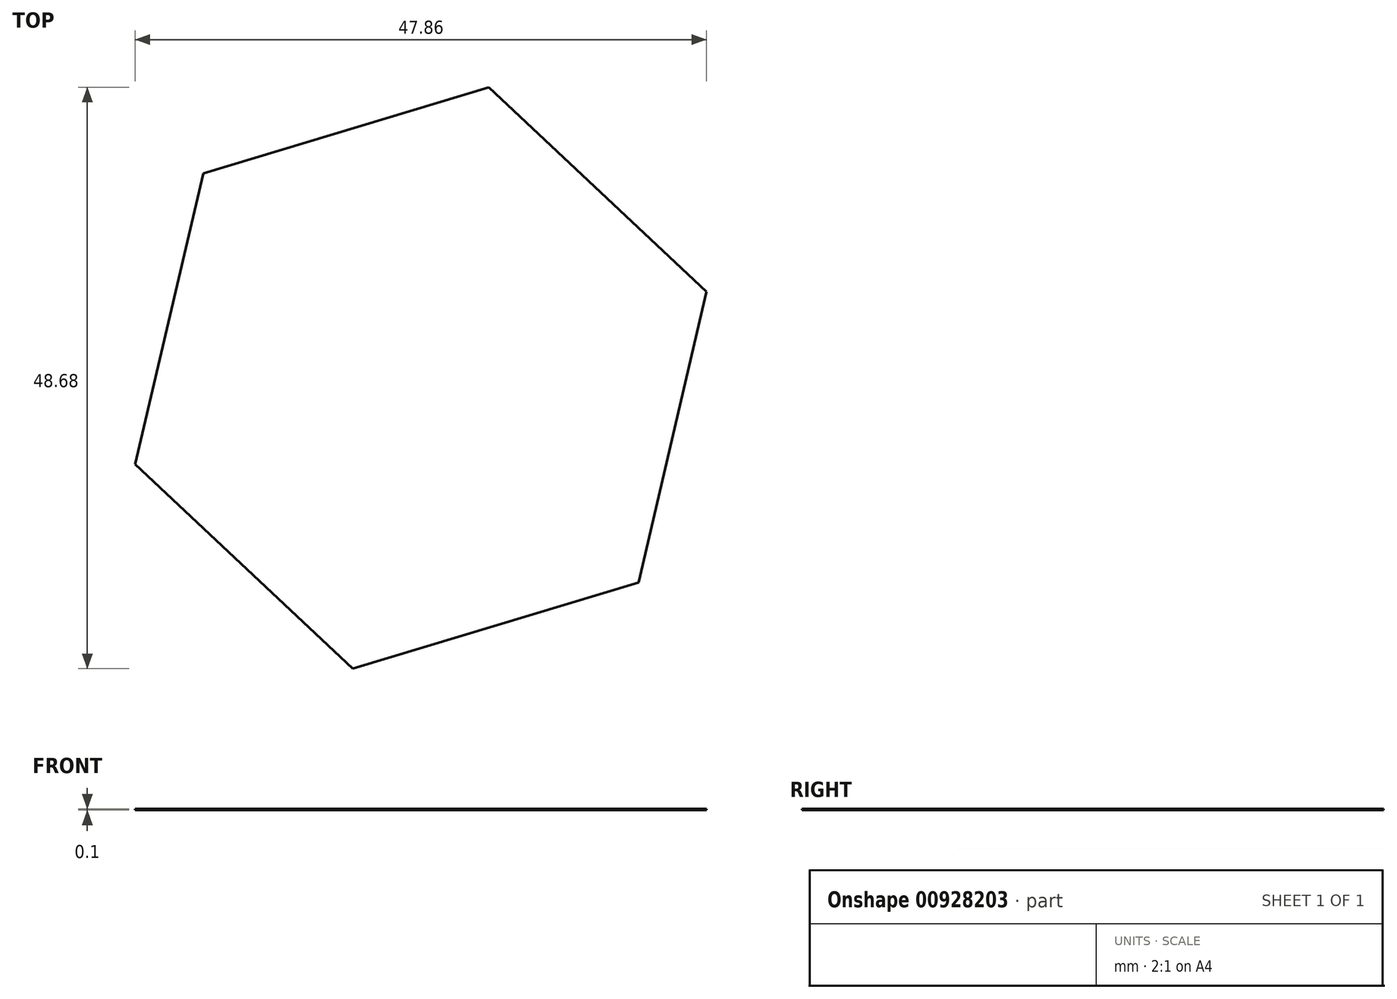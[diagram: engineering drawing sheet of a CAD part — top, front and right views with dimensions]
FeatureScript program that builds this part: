
annotation { "Feature Type Name" : "Feature", "Feature Type Description" : "" }
export const myFeature = defineFeature(function(context is Context, id is Id, definition is map)
    precondition{}
    {
        {
            var Q0;
            Q0=qCreatedBy(makeId("Top.planeOp"),FACE);
            var sketch = newSketch(context, id + "F0", { "sketchPlane" : qUnion([Q0])});
            skCircle(sketch, "E0.cCircle", {"center": v(0, 0) * mm, "radius": 21.65 * mm, "construction": true});
            skLineSegment(sketch, "E0.0", {"start": v(18.22, -17.11) * mm, "end": v(-5.71, -24.34) * mm});
            skLineSegment(sketch, "E0.1", {"start": v(-5.71, -24.34) * mm, "end": v(-23.93, -7.22) * mm});
            skLineSegment(sketch, "E0.2", {"start": v(-23.93, -7.22) * mm, "end": v(-18.22, 17.11) * mm});
            skLineSegment(sketch, "E0.3", {"start": v(-18.22, 17.11) * mm, "end": v(5.71, 24.34) * mm});
            skLineSegment(sketch, "E0.4", {"start": v(5.71, 24.34) * mm, "end": v(23.93, 7.22) * mm});
            skLineSegment(sketch, "E0.5", {"start": v(23.93, 7.22) * mm, "end": v(18.22, -17.11) * mm});
            skPoint(sketch, "E0.0.midPoint", {"position": v(6.26, -20.73) * mm});
            skSolve(sketch);
        }
        {
            var Q0;
            Q0=makeQuery(id+"F0.imprint","IMPRINT",FACE,{"disambiguationData":[TD([[makeQuery(id+"F0.imprint","IMPRINT",EDGE,{"derivedFrom":sQuery(id+"F0.wireOp",EDGE,"E0.0")}),-1.0]])]});
            extrude(context, id + "F1", {"entities" : qUnion([Q0]), "depth" : 0.1 * mm, "offsetDistance" : 25 * mm});
        }
    });
